# Revit family: 2-6184-24 Echo
name_source: partatom
category: Lighting Fixtures
revit_build: Autodesk Revit LT 2014 (Build: 20130308_1515(x64)
units: mm (PartAtom-declared; Revit-internal decimal feet)

## types (1)
- 2-6184-24 Echo
    Apparent Load = 27 VA
    Ballast Manufacturer = Fulham
    Color Filter = 16777215
    Default Elevation = 4' - 0"
    Description = 11 1/2"dia. Ceiling Mount
    Diffuser = Matte White Acrylic
    Dimming Lamp Color Temperature Shift = <None>
    Emit Shape Visible in Rendering = No
    Emit from Circle Diameter = 2' - 0"
    Fixture Diameter = 0' - 11 5/8"
    Input Current = Antron CSD-UV18PS
    Input Power = 27.3
    Input Voltage = 120V
    Junction Box = 4" Octagonal
    Lamp = 2x13W quad tube 4-pin (G24-1) fluorescent
    Lamp Manufacturer = Sylvania
    Manufacturer = Oxygen Lighting
    Metal Finish = Satin Nickel
    Model = 2-6184-24
    Photometric Web File = 2-6184-24.IES
    Power Factor = 0.99
    Shade = White Grass Shade
    Tilt Angle = -90.00°
    Type Comments = Lighting - Fluorescent
    URL = http:www//oxygenlighting.com

## geometry (parser evidence)
native form markers: Sweep x1
no freeform markers — native parametric forms only
